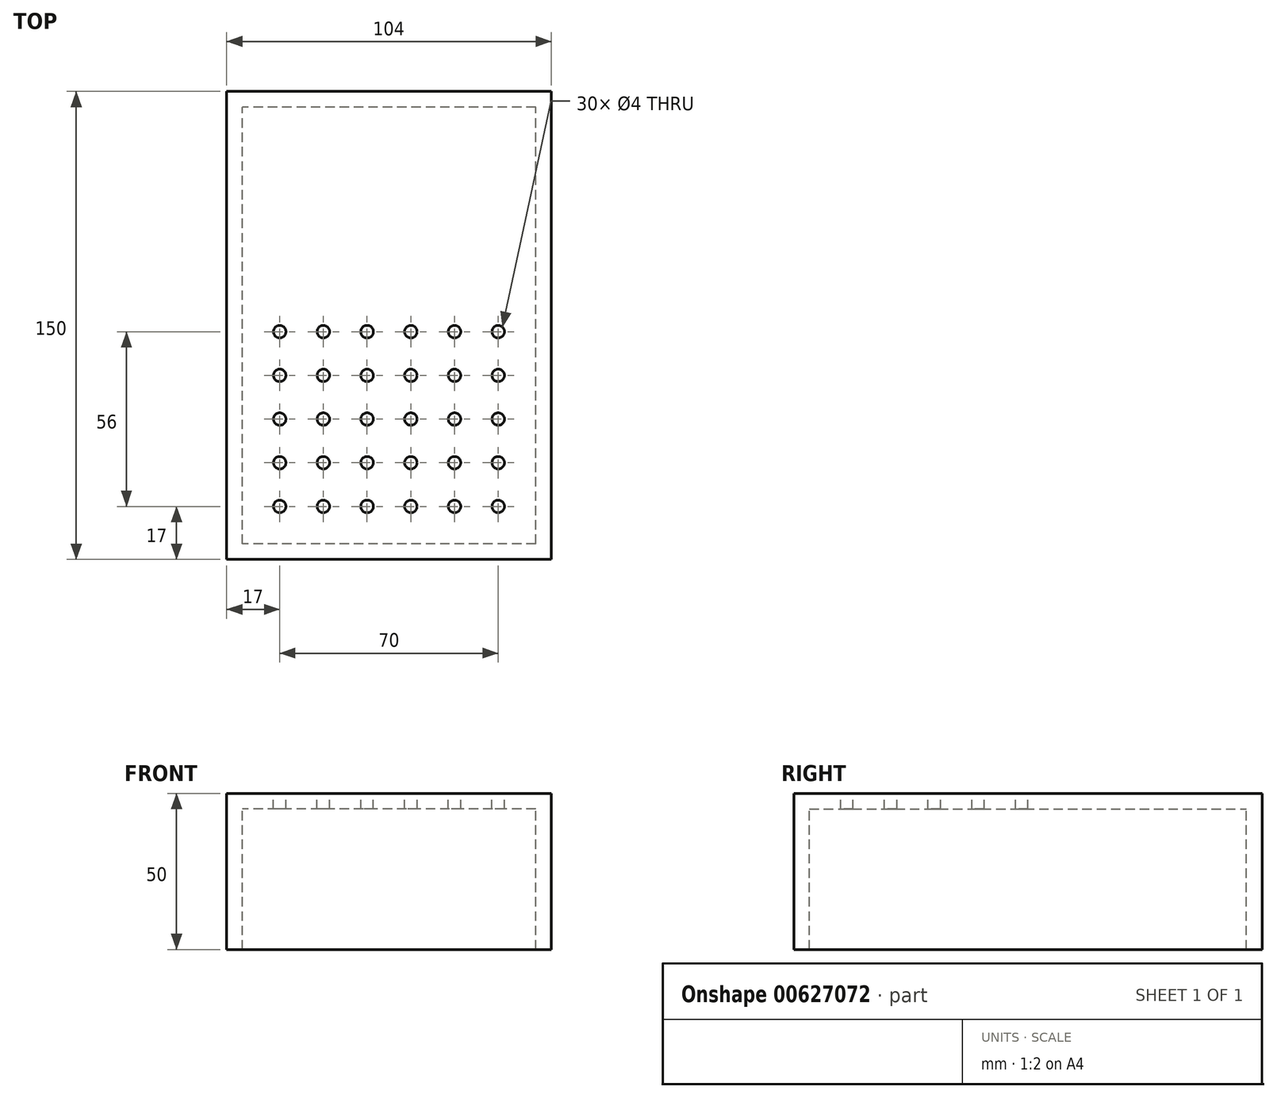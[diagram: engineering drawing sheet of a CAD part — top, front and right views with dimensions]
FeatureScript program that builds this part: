
annotation { "Feature Type Name" : "Feature", "Feature Type Description" : "" }
export const myFeature = defineFeature(function(context is Context, id is Id, definition is map)
    precondition{}
    {
        {
            var Q0;
            Q0=qCreatedBy(makeId("Top.planeOp"),FACE);
            var sketch = newSketch(context, id + "F0", { "sketchPlane" : qUnion([Q0])});
            skPoint(sketch, "E0.middle", {"position": v(0, 0) * mm});
            skCircle(sketch, "E1", {"center": v(-35, 28) * mm, "radius": 2 * mm});
            skCircle(sketch, "E2.0.1.0", {"center": v(-35, 14) * mm, "radius": 2 * mm});
            skCircle(sketch, "E2.0.2.0", {"center": v(-35, 0) * mm, "radius": 2 * mm});
            skCircle(sketch, "E2.0.3.0", {"center": v(-35, -14) * mm, "radius": 2 * mm});
            skCircle(sketch, "E2.0.4.0", {"center": v(-35, -28) * mm, "radius": 2 * mm});
            skCircle(sketch, "E2.1.0.0", {"center": v(-21, 28) * mm, "radius": 2 * mm});
            skCircle(sketch, "E2.1.1.0", {"center": v(-21, 14) * mm, "radius": 2 * mm});
            skCircle(sketch, "E2.1.2.0", {"center": v(-21, 0) * mm, "radius": 2 * mm});
            skCircle(sketch, "E2.1.3.0", {"center": v(-21, -14) * mm, "radius": 2 * mm});
            skCircle(sketch, "E2.1.4.0", {"center": v(-21, -28) * mm, "radius": 2 * mm});
            skCircle(sketch, "E2.2.0.0", {"center": v(-7, 28) * mm, "radius": 2 * mm});
            skCircle(sketch, "E2.2.1.0", {"center": v(-7, 14) * mm, "radius": 2 * mm});
            skCircle(sketch, "E2.2.2.0", {"center": v(-7, 0) * mm, "radius": 2 * mm});
            skCircle(sketch, "E2.2.3.0", {"center": v(-7, -14) * mm, "radius": 2 * mm});
            skCircle(sketch, "E2.2.4.0", {"center": v(-7, -28) * mm, "radius": 2 * mm});
            skCircle(sketch, "E2.3.0.0", {"center": v(7, 28) * mm, "radius": 2 * mm});
            skCircle(sketch, "E2.3.1.0", {"center": v(7, 14) * mm, "radius": 2 * mm});
            skCircle(sketch, "E2.3.2.0", {"center": v(7, 0) * mm, "radius": 2 * mm});
            skCircle(sketch, "E2.3.3.0", {"center": v(7, -14) * mm, "radius": 2 * mm});
            skCircle(sketch, "E2.3.4.0", {"center": v(7, -28) * mm, "radius": 2 * mm});
            skCircle(sketch, "E2.4.0.0", {"center": v(21, 28) * mm, "radius": 2 * mm});
            skCircle(sketch, "E2.4.1.0", {"center": v(21, 14) * mm, "radius": 2 * mm});
            skCircle(sketch, "E2.4.2.0", {"center": v(21, 0) * mm, "radius": 2 * mm});
            skCircle(sketch, "E2.4.3.0", {"center": v(21, -14) * mm, "radius": 2 * mm});
            skCircle(sketch, "E2.4.4.0", {"center": v(21, -28) * mm, "radius": 2 * mm});
            skCircle(sketch, "E2.5.0.0", {"center": v(35, 28) * mm, "radius": 2 * mm});
            skCircle(sketch, "E2.5.1.0", {"center": v(35, 14) * mm, "radius": 2 * mm});
            skCircle(sketch, "E2.5.2.0", {"center": v(35, 0) * mm, "radius": 2 * mm});
            skCircle(sketch, "E2.5.3.0", {"center": v(35, -14) * mm, "radius": 2 * mm});
            skCircle(sketch, "E2.5.4.0", {"center": v(35, -28) * mm, "radius": 2 * mm});
            skLineSegment(sketch, "E2.direction1", {"start": v(-35, 28) * mm, "end": v(-21, 28) * mm, "construction": true});
            skLineSegment(sketch, "E2.direction2", {"start": v(-35, 28) * mm, "end": v(-35, 14) * mm, "construction": true});
            skLineSegment(sketch, "E3.bottom", {"start": v(52, -45) * mm, "end": v(-52, -45) * mm});
            skLineSegment(sketch, "E3.top", {"start": v(52, 105) * mm, "end": v(-52, 105) * mm});
            skLineSegment(sketch, "E3.left", {"start": v(52, -45) * mm, "end": v(52, 105) * mm});
            skLineSegment(sketch, "E3.right", {"start": v(-52, -45) * mm, "end": v(-52, 105) * mm});
            skPoint(sketch, "E3.middle", {"position": v(0, 30) * mm});
            skSolve(sketch);
        }
        {
            var Q0;
            Q0=makeQuery(id+"F0.imprint","IMPRINT",FACE,{"disambiguationData":[TD([[makeQuery(id+"F0.imprint","IMPRINT",EDGE,{"derivedFrom":sQuery(id+"F0.wireOp",EDGE,"E0.bottom")}),-1.0]])]});
            var Q1;
            Q1=makeQuery(id+"F0.imprint","IMPRINT",FACE,{"disambiguationData":[TD([[makeQuery(id+"F0.imprint","IMPRINT",EDGE,{"derivedFrom":sQuery(id+"F0.wireOp",EDGE,"E2.3.4.0")}),1.0]])]});
            var Q2;
            Q2=makeQuery(id+"F0.imprint","IMPRINT",FACE,{"disambiguationData":[TD([[makeQuery(id+"F0.imprint","IMPRINT",EDGE,{"derivedFrom":sQuery(id+"F0.wireOp",EDGE,"E2.5.1.0")}),1.0]])]});
            var Q3;
            Q3=makeQuery(id+"F0.imprint","IMPRINT",FACE,{"disambiguationData":[TD([[makeQuery(id+"F0.imprint","IMPRINT",EDGE,{"derivedFrom":sQuery(id+"F0.wireOp",EDGE,"E2.4.2.0")}),1.0]])]});
            var Q4;
            Q4=makeQuery(id+"F0.imprint","IMPRINT",FACE,{"disambiguationData":[TD([[makeQuery(id+"F0.imprint","IMPRINT",EDGE,{"derivedFrom":sQuery(id+"F0.wireOp",EDGE,"E2.4.0.0")}),1.0]])]});
            var Q5;
            Q5=makeQuery(id+"F0.imprint","IMPRINT",FACE,{"disambiguationData":[TD([[makeQuery(id+"F0.imprint","IMPRINT",EDGE,{"derivedFrom":sQuery(id+"F0.wireOp",EDGE,"E2.3.0.0")}),1.0]])]});
            var Q6;
            Q6=makeQuery(id+"F0.imprint","IMPRINT",FACE,{"disambiguationData":[TD([[makeQuery(id+"F0.imprint","IMPRINT",EDGE,{"derivedFrom":sQuery(id+"F0.wireOp",EDGE,"E2.5.4.0")}),1.0]])]});
            var Q7;
            Q7=makeQuery(id+"F0.imprint","IMPRINT",FACE,{"disambiguationData":[TD([[makeQuery(id+"F0.imprint","IMPRINT",EDGE,{"derivedFrom":sQuery(id+"F0.wireOp",EDGE,"E2.2.3.0")}),1.0]])]});
            var Q8;
            Q8=makeQuery(id+"F0.imprint","IMPRINT",FACE,{"disambiguationData":[TD([[makeQuery(id+"F0.imprint","IMPRINT",EDGE,{"derivedFrom":sQuery(id+"F0.wireOp",EDGE,"E2.2.4.0")}),1.0]])]});
            var Q9;
            Q9=makeQuery(id+"F0.imprint","IMPRINT",FACE,{"disambiguationData":[TD([[makeQuery(id+"F0.imprint","IMPRINT",EDGE,{"derivedFrom":sQuery(id+"F0.wireOp",EDGE,"E2.3.1.0")}),1.0]])]});
            var Q10;
            Q10=makeQuery(id+"F0.imprint","IMPRINT",FACE,{"disambiguationData":[TD([[makeQuery(id+"F0.imprint","IMPRINT",EDGE,{"derivedFrom":sQuery(id+"F0.wireOp",EDGE,"E1")}),1.0]])]});
            var Q11;
            Q11=makeQuery(id+"F0.imprint","IMPRINT",FACE,{"disambiguationData":[TD([[makeQuery(id+"F0.imprint","IMPRINT",EDGE,{"derivedFrom":sQuery(id+"F0.wireOp",EDGE,"E2.0.1.0")}),1.0]])]});
            var Q12;
            Q12=makeQuery(id+"F0.imprint","IMPRINT",FACE,{"disambiguationData":[TD([[makeQuery(id+"F0.imprint","IMPRINT",EDGE,{"derivedFrom":sQuery(id+"F0.wireOp",EDGE,"E2.0.2.0")}),1.0]])]});
            var Q13;
            Q13=makeQuery(id+"F0.imprint","IMPRINT",FACE,{"disambiguationData":[TD([[makeQuery(id+"F0.imprint","IMPRINT",EDGE,{"derivedFrom":sQuery(id+"F0.wireOp",EDGE,"E2.0.3.0")}),1.0]])]});
            var Q14;
            Q14=makeQuery(id+"F0.imprint","IMPRINT",FACE,{"disambiguationData":[TD([[makeQuery(id+"F0.imprint","IMPRINT",EDGE,{"derivedFrom":sQuery(id+"F0.wireOp",EDGE,"E2.0.4.0")}),1.0]])]});
            var Q15;
            Q15=makeQuery(id+"F0.imprint","IMPRINT",FACE,{"disambiguationData":[TD([[makeQuery(id+"F0.imprint","IMPRINT",EDGE,{"derivedFrom":sQuery(id+"F0.wireOp",EDGE,"E2.1.0.0")}),1.0]])]});
            var Q16;
            Q16=makeQuery(id+"F0.imprint","IMPRINT",FACE,{"disambiguationData":[TD([[makeQuery(id+"F0.imprint","IMPRINT",EDGE,{"derivedFrom":sQuery(id+"F0.wireOp",EDGE,"E2.1.1.0")}),1.0]])]});
            var Q17;
            Q17=makeQuery(id+"F0.imprint","IMPRINT",FACE,{"disambiguationData":[TD([[makeQuery(id+"F0.imprint","IMPRINT",EDGE,{"derivedFrom":sQuery(id+"F0.wireOp",EDGE,"E2.1.2.0")}),1.0]])]});
            var Q18;
            Q18=makeQuery(id+"F0.imprint","IMPRINT",FACE,{"disambiguationData":[TD([[makeQuery(id+"F0.imprint","IMPRINT",EDGE,{"derivedFrom":sQuery(id+"F0.wireOp",EDGE,"E2.1.3.0")}),1.0]])]});
            var Q19;
            Q19=makeQuery(id+"F0.imprint","IMPRINT",FACE,{"disambiguationData":[TD([[makeQuery(id+"F0.imprint","IMPRINT",EDGE,{"derivedFrom":sQuery(id+"F0.wireOp",EDGE,"E2.1.4.0")}),1.0]])]});
            var Q20;
            Q20=makeQuery(id+"F0.imprint","IMPRINT",FACE,{"disambiguationData":[TD([[makeQuery(id+"F0.imprint","IMPRINT",EDGE,{"derivedFrom":sQuery(id+"F0.wireOp",EDGE,"E2.2.0.0")}),1.0]])]});
            var Q21;
            Q21=makeQuery(id+"F0.imprint","IMPRINT",FACE,{"disambiguationData":[TD([[makeQuery(id+"F0.imprint","IMPRINT",EDGE,{"derivedFrom":sQuery(id+"F0.wireOp",EDGE,"E2.2.1.0")}),1.0]])]});
            var Q22;
            Q22=makeQuery(id+"F0.imprint","IMPRINT",FACE,{"disambiguationData":[TD([[makeQuery(id+"F0.imprint","IMPRINT",EDGE,{"derivedFrom":sQuery(id+"F0.wireOp",EDGE,"E2.2.2.0")}),1.0]])]});
            var Q23;
            Q23=makeQuery(id+"F0.imprint","IMPRINT",FACE,{"disambiguationData":[TD([[makeQuery(id+"F0.imprint","IMPRINT",EDGE,{"derivedFrom":sQuery(id+"F0.wireOp",EDGE,"E2.5.2.0")}),1.0]])]});
            var Q24;
            Q24=makeQuery(id+"F0.imprint","IMPRINT",FACE,{"disambiguationData":[TD([[makeQuery(id+"F0.imprint","IMPRINT",EDGE,{"derivedFrom":sQuery(id+"F0.wireOp",EDGE,"E2.4.3.0")}),1.0]])]});
            var Q25;
            Q25=makeQuery(id+"F0.imprint","IMPRINT",FACE,{"disambiguationData":[TD([[makeQuery(id+"F0.imprint","IMPRINT",EDGE,{"derivedFrom":sQuery(id+"F0.wireOp",EDGE,"E2.4.1.0")}),1.0]])]});
            var Q26;
            Q26=makeQuery(id+"F0.imprint","IMPRINT",FACE,{"disambiguationData":[TD([[makeQuery(id+"F0.imprint","IMPRINT",EDGE,{"derivedFrom":sQuery(id+"F0.wireOp",EDGE,"E2.3.2.0")}),1.0]])]});
            var Q27;
            Q27=makeQuery(id+"F0.imprint","IMPRINT",FACE,{"disambiguationData":[TD([[makeQuery(id+"F0.imprint","IMPRINT",EDGE,{"derivedFrom":sQuery(id+"F0.wireOp",EDGE,"E2.5.3.0")}),1.0]])]});
            var Q28;
            Q28=makeQuery(id+"F0.imprint","IMPRINT",FACE,{"disambiguationData":[TD([[makeQuery(id+"F0.imprint","IMPRINT",EDGE,{"derivedFrom":sQuery(id+"F0.wireOp",EDGE,"E2.4.4.0")}),1.0]])]});
            var Q29;
            Q29=makeQuery(id+"F0.imprint","IMPRINT",FACE,{"disambiguationData":[TD([[makeQuery(id+"F0.imprint","IMPRINT",EDGE,{"derivedFrom":sQuery(id+"F0.wireOp",EDGE,"E2.3.3.0")}),1.0]])]});
            var Q30;
            Q30=makeQuery(id+"F0.imprint","IMPRINT",FACE,{"disambiguationData":[TD([[makeQuery(id+"F0.imprint","IMPRINT",EDGE,{"derivedFrom":sQuery(id+"F0.wireOp",EDGE,"E2.5.0.0")}),1.0]])]});
            var Q31;
            Q31=makeQuery(id+"F0.imprint","IMPRINT",FACE,{"disambiguationData":[TD([[makeQuery(id+"F0.imprint","IMPRINT",EDGE,{"derivedFrom":sQuery(id+"F0.wireOp",EDGE,"E1")}),-1.0]])]});
            extrude(context, id + "F1", {"entities" : qUnion([Q0, Q1, Q2, Q3, Q4, Q5, Q6, Q7, Q8, Q9, Q10, Q11, Q12, Q13, Q14, Q15, Q16, Q17, Q18, Q19, Q20, Q21, Q22, Q23, Q24, Q25, Q26, Q27, Q28, Q29, Q30, Q31]), "oppositeDirection" : true, "depth" : 50 * mm, "offsetDistance" : 25 * mm});
        }
        {
            var Q0;
            Q0=makeQuery(id+"F1.opExtrude","CAP_FACE",FACE,{"disambiguationData":[OSD([sQuery(id+"F0.wireOp",EDGE,"E3.bottom"),sQuery(id+"F0.wireOp",EDGE,"E3.top"),sQuery(id+"F0.wireOp",EDGE,"E3.left"),sQuery(id+"F0.wireOp",EDGE,"E3.right")])],"isStart":false});
            shell(context, id + "F2", {"entities" : qUnion([Q0]), "thickness" : 5 * mm});
        }
        {
            var Q0;
            Q0=makeQuery(id+"F0.imprint","IMPRINT",FACE,{"disambiguationData":[TD([[makeQuery(id+"F0.imprint","IMPRINT",EDGE,{"derivedFrom":sQuery(id+"F0.wireOp",EDGE,"E2.3.3.0")}),1.0]])]});
            var Q1;
            Q1=makeQuery(id+"F0.imprint","IMPRINT",FACE,{"disambiguationData":[TD([[makeQuery(id+"F0.imprint","IMPRINT",EDGE,{"derivedFrom":sQuery(id+"F0.wireOp",EDGE,"E2.5.3.0")}),1.0]])]});
            var Q2;
            Q2=makeQuery(id+"F0.imprint","IMPRINT",FACE,{"disambiguationData":[TD([[makeQuery(id+"F0.imprint","IMPRINT",EDGE,{"derivedFrom":sQuery(id+"F0.wireOp",EDGE,"E2.4.4.0")}),1.0]])]});
            var Q3;
            Q3=makeQuery(id+"F0.imprint","IMPRINT",FACE,{"disambiguationData":[TD([[makeQuery(id+"F0.imprint","IMPRINT",EDGE,{"derivedFrom":sQuery(id+"F0.wireOp",EDGE,"E2.3.2.0")}),1.0]])]});
            var Q4;
            Q4=makeQuery(id+"F0.imprint","IMPRINT",FACE,{"disambiguationData":[TD([[makeQuery(id+"F0.imprint","IMPRINT",EDGE,{"derivedFrom":sQuery(id+"F0.wireOp",EDGE,"E2.4.1.0")}),1.0]])]});
            var Q5;
            Q5=makeQuery(id+"F0.imprint","IMPRINT",FACE,{"disambiguationData":[TD([[makeQuery(id+"F0.imprint","IMPRINT",EDGE,{"derivedFrom":sQuery(id+"F0.wireOp",EDGE,"E2.4.3.0")}),1.0]])]});
            var Q6;
            Q6=makeQuery(id+"F0.imprint","IMPRINT",FACE,{"disambiguationData":[TD([[makeQuery(id+"F0.imprint","IMPRINT",EDGE,{"derivedFrom":sQuery(id+"F0.wireOp",EDGE,"E2.5.2.0")}),1.0]])]});
            var Q7;
            Q7=makeQuery(id+"F0.imprint","IMPRINT",FACE,{"disambiguationData":[TD([[makeQuery(id+"F0.imprint","IMPRINT",EDGE,{"derivedFrom":sQuery(id+"F0.wireOp",EDGE,"E2.2.2.0")}),1.0]])]});
            var Q8;
            Q8=makeQuery(id+"F0.imprint","IMPRINT",FACE,{"disambiguationData":[TD([[makeQuery(id+"F0.imprint","IMPRINT",EDGE,{"derivedFrom":sQuery(id+"F0.wireOp",EDGE,"E2.2.1.0")}),1.0]])]});
            var Q9;
            Q9=makeQuery(id+"F0.imprint","IMPRINT",FACE,{"disambiguationData":[TD([[makeQuery(id+"F0.imprint","IMPRINT",EDGE,{"derivedFrom":sQuery(id+"F0.wireOp",EDGE,"E2.2.0.0")}),1.0]])]});
            var Q10;
            Q10=makeQuery(id+"F0.imprint","IMPRINT",FACE,{"disambiguationData":[TD([[makeQuery(id+"F0.imprint","IMPRINT",EDGE,{"derivedFrom":sQuery(id+"F0.wireOp",EDGE,"E2.1.4.0")}),1.0]])]});
            var Q11;
            Q11=makeQuery(id+"F0.imprint","IMPRINT",FACE,{"disambiguationData":[TD([[makeQuery(id+"F0.imprint","IMPRINT",EDGE,{"derivedFrom":sQuery(id+"F0.wireOp",EDGE,"E2.1.3.0")}),1.0]])]});
            var Q12;
            Q12=makeQuery(id+"F0.imprint","IMPRINT",FACE,{"disambiguationData":[TD([[makeQuery(id+"F0.imprint","IMPRINT",EDGE,{"derivedFrom":sQuery(id+"F0.wireOp",EDGE,"E2.1.2.0")}),1.0]])]});
            var Q13;
            Q13=makeQuery(id+"F0.imprint","IMPRINT",FACE,{"disambiguationData":[TD([[makeQuery(id+"F0.imprint","IMPRINT",EDGE,{"derivedFrom":sQuery(id+"F0.wireOp",EDGE,"E2.1.1.0")}),1.0]])]});
            var Q14;
            Q14=makeQuery(id+"F0.imprint","IMPRINT",FACE,{"disambiguationData":[TD([[makeQuery(id+"F0.imprint","IMPRINT",EDGE,{"derivedFrom":sQuery(id+"F0.wireOp",EDGE,"E2.0.4.0")}),1.0]])]});
            var Q15;
            Q15=makeQuery(id+"F0.imprint","IMPRINT",FACE,{"disambiguationData":[TD([[makeQuery(id+"F0.imprint","IMPRINT",EDGE,{"derivedFrom":sQuery(id+"F0.wireOp",EDGE,"E2.0.3.0")}),1.0]])]});
            var Q16;
            Q16=makeQuery(id+"F0.imprint","IMPRINT",FACE,{"disambiguationData":[TD([[makeQuery(id+"F0.imprint","IMPRINT",EDGE,{"derivedFrom":sQuery(id+"F0.wireOp",EDGE,"E2.0.2.0")}),1.0]])]});
            var Q17;
            Q17=makeQuery(id+"F0.imprint","IMPRINT",FACE,{"disambiguationData":[TD([[makeQuery(id+"F0.imprint","IMPRINT",EDGE,{"derivedFrom":sQuery(id+"F0.wireOp",EDGE,"E2.3.1.0")}),1.0]])]});
            var Q18;
            Q18=makeQuery(id+"F0.imprint","IMPRINT",FACE,{"disambiguationData":[TD([[makeQuery(id+"F0.imprint","IMPRINT",EDGE,{"derivedFrom":sQuery(id+"F0.wireOp",EDGE,"E2.2.4.0")}),1.0]])]});
            var Q19;
            Q19=makeQuery(id+"F0.imprint","IMPRINT",FACE,{"disambiguationData":[TD([[makeQuery(id+"F0.imprint","IMPRINT",EDGE,{"derivedFrom":sQuery(id+"F0.wireOp",EDGE,"E2.2.3.0")}),1.0]])]});
            var Q20;
            Q20=makeQuery(id+"F0.imprint","IMPRINT",FACE,{"disambiguationData":[TD([[makeQuery(id+"F0.imprint","IMPRINT",EDGE,{"derivedFrom":sQuery(id+"F0.wireOp",EDGE,"E2.3.0.0")}),1.0]])]});
            var Q21;
            Q21=makeQuery(id+"F0.imprint","IMPRINT",FACE,{"disambiguationData":[TD([[makeQuery(id+"F0.imprint","IMPRINT",EDGE,{"derivedFrom":sQuery(id+"F0.wireOp",EDGE,"E2.5.4.0")}),1.0]])]});
            var Q22;
            Q22=makeQuery(id+"F0.imprint","IMPRINT",FACE,{"disambiguationData":[TD([[makeQuery(id+"F0.imprint","IMPRINT",EDGE,{"derivedFrom":sQuery(id+"F0.wireOp",EDGE,"E2.4.0.0")}),1.0]])]});
            var Q23;
            Q23=makeQuery(id+"F0.imprint","IMPRINT",FACE,{"disambiguationData":[TD([[makeQuery(id+"F0.imprint","IMPRINT",EDGE,{"derivedFrom":sQuery(id+"F0.wireOp",EDGE,"E2.4.2.0")}),1.0]])]});
            var Q24;
            Q24=makeQuery(id+"F0.imprint","IMPRINT",FACE,{"disambiguationData":[TD([[makeQuery(id+"F0.imprint","IMPRINT",EDGE,{"derivedFrom":sQuery(id+"F0.wireOp",EDGE,"E2.5.1.0")}),1.0]])]});
            var Q25;
            Q25=makeQuery(id+"F0.imprint","IMPRINT",FACE,{"disambiguationData":[TD([[makeQuery(id+"F0.imprint","IMPRINT",EDGE,{"derivedFrom":sQuery(id+"F0.wireOp",EDGE,"E2.3.4.0")}),1.0]])]});
            var Q26;
            Q26=makeQuery(id+"F0.imprint","IMPRINT",FACE,{"disambiguationData":[TD([[makeQuery(id+"F0.imprint","IMPRINT",EDGE,{"derivedFrom":sQuery(id+"F0.wireOp",EDGE,"E2.5.0.0")}),1.0]])]});
            var Q27;
            Q27=makeQuery(id+"F0.imprint","IMPRINT",FACE,{"disambiguationData":[TD([[makeQuery(id+"F0.imprint","IMPRINT",EDGE,{"derivedFrom":sQuery(id+"F0.wireOp",EDGE,"E2.1.0.0")}),1.0]])]});
            var Q28;
            Q28=makeQuery(id+"F0.imprint","IMPRINT",FACE,{"disambiguationData":[TD([[makeQuery(id+"F0.imprint","IMPRINT",EDGE,{"derivedFrom":sQuery(id+"F0.wireOp",EDGE,"E2.0.1.0")}),1.0]])]});
            var Q29;
            Q29=makeQuery(id+"F0.imprint","IMPRINT",FACE,{"disambiguationData":[TD([[makeQuery(id+"F0.imprint","IMPRINT",EDGE,{"derivedFrom":sQuery(id+"F0.wireOp",EDGE,"E1")}),1.0]])]});
            extrude(context, id + "F3", {"entities" : qUnion([Q0, Q1, Q2, Q3, Q4, Q5, Q6, Q7, Q8, Q9, Q10, Q11, Q12, Q13, Q14, Q15, Q16, Q17, Q18, Q19, Q20, Q21, Q22, Q23, Q24, Q25, Q26, Q27, Q28, Q29]), "operationType" : NewBodyOperationType.REMOVE, "oppositeDirection" : true, "depth" : 25 * mm, "offsetDistance" : 25 * mm});
        }
    });
